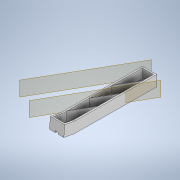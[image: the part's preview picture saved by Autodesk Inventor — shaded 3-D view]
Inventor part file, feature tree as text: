
AUTODESK INVENTOR PART (.ipt)
format: ipt  version: 2020.3 (Build 243373000, 373)  size: 177,664 bytes
history: native  units: mm
features: sketch x3, plane x2, sweep x1, shell x1, rib x1, pattern_linear x1, projected_geometry x1
ambient origin geometry x8: Origin, YZ Plane, XZ Plane, XY Plane, X Axis, Y Axis, Z Axis, Center Point
bodies: Solid1 (feature_tree)
feature tree (10):
  sweep  "Sweep1"
  shell  "Shell1"  Thickness=22.274605mm
  plane  "Work Plane3"
  rib  "Rib1"
  pattern_linear  "Rectangular Pattern1"  Spacing1=29.670597mm  [1 undecoded]
  sketch  "Sketch1"  dims[d0=2.324306mm d1=4.609875mm d2=22.274605mm]
  sketch  "Sketch2"  dims[d3=16.580053mm]
  plane  "Work Plane2"
  sketch  "Sketch6"  dims[d5=0.087266mm d6=29.670597mm d7=0.0mm d8=0.0mm d9=2.5mm d11=-10.471976mm d12=40.25mm d13=10.0mm d14=1.0mm d15=0.0mm d16=0.0mm d17=1.0mm d18=1.0mm d19=30.0mm d21=35.0mm]
  projected_geometry  "Projected Loop3"
note: 1 required parameter value undecoded (feature->parameter linkage not recoverable at this tier; creation-order binding heuristic only, values carry confidence <= 0.55)
